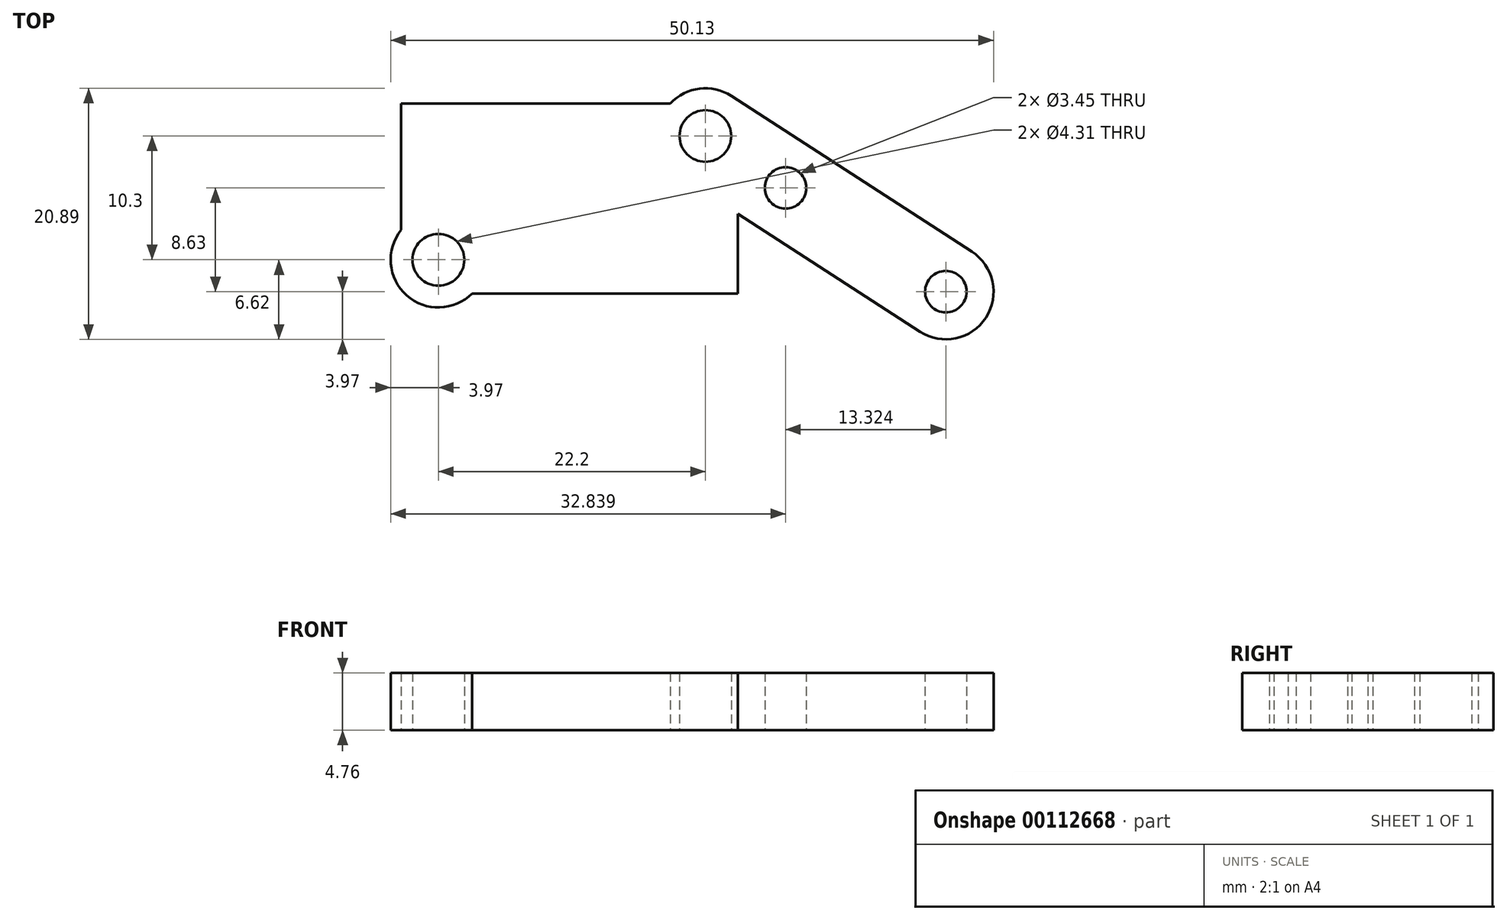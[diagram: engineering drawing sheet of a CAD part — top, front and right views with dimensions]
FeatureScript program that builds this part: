
annotation { "Feature Type Name" : "Feature", "Feature Type Description" : "" }
export const myFeature = defineFeature(function(context is Context, id is Id, definition is map)
    precondition{}
    {
        {
            var Q0;
            Q0=qCreatedBy(makeId("Top.planeOp"),FACE);
            var sketch = newSketch(context, id + "F0", { "sketchPlane" : qUnion([Q0])});
            skLineSegment(sketch, "E0.left", {"start": v(0, 0) * mm, "end": v(0, -10.52) * mm});
            skLineSegment(sketch, "E1", {"start": v(25.3, 0) * mm, "end": v(25.3, -2.7) * mm, "construction": true});
            skLineSegment(sketch, "E2", {"start": v(3.1, -15.8) * mm, "end": v(3.1, -13) * mm, "construction": true});
            skLineSegment(sketch, "E3", {"start": v(3.1, -13) * mm, "end": v(0, -13) * mm, "construction": true});
            skCircle(sketch, "E4", {"center": v(3.1, -13) * mm, "radius": 2.15 * mm});
            skCircle(sketch, "E5", {"center": v(25.3, -2.7) * mm, "radius": 2.15 * mm});
            skLineSegment(sketch, "E6", {"start": v(5.91, -15.8) * mm, "end": v(28, -15.8) * mm});
            skLineSegment(sketch, "E7", {"start": v(0, 0) * mm, "end": v(22.4, 0) * mm});
            skLineSegment(sketch, "E8", {"start": v(25.3, -2.7) * mm, "end": v(3.1, -2.7) * mm, "construction": true});
            skLineSegment(sketch, "E9", {"start": v(3.1, -2.7) * mm, "end": v(3.1, -13) * mm, "construction": true});
            skLineSegment(sketch, "E10", {"start": v(27.46, 0.63) * mm, "end": v(47.45, -12.32) * mm});
            skLineSegment(sketch, "E11", {"start": v(47.45, -12.32) * mm, "end": v(43.14, -18.98) * mm, "construction": true});
            skLineSegment(sketch, "E12", {"start": v(43.14, -18.98) * mm, "end": v(28, -9.18) * mm});
            skLineSegment(sketch, "E13", {"start": v(28, -9.18) * mm, "end": v(28, -15.8) * mm});
            skCircle(sketch, "E14", {"center": v(31.97, -7.02) * mm, "radius": 3.97 * mm, "construction": true});
            skLineSegment(sketch, "E15", {"start": v(31.97, -7.02) * mm, "end": v(45.3, -15.65) * mm, "construction": true});
            skArc(sketch, "E16", {"start": v(43.14, -18.98) * mm, "mid": v(48.62, -17.8) * mm, "end": v(47.45, -12.32) * mm});
            skCircle(sketch, "E17", {"center": v(45.3, -15.65) * mm, "radius": 1.73 * mm});
            skCircle(sketch, "E18", {"center": v(31.97, -7.02) * mm, "radius": 1.73 * mm});
            skArc(sketch, "E19", {"start": v(0, -10.52) * mm, "mid": v(0.46, -15.96) * mm, "end": v(5.91, -15.8) * mm});
            skArc(sketch, "E20", {"start": v(27.46, 0.63) * mm, "mid": v(24.8, 1.24) * mm, "end": v(22.4, 0) * mm});
            skSolve(sketch);
        }
        {
            var Q0;
            Q0=makeQuery(id+"F0.imprint","IMPRINT",FACE,{"disambiguationData":[TD([[makeQuery(id+"F0.imprint","IMPRINT",EDGE,{"derivedFrom":sQuery(id+"F0.wireOp",EDGE,"E0.bottom")}),-1.0]])]});
            var Q1;
            Q1=makeQuery(id+"F0.imprint","IMPRINT",FACE,{"disambiguationData":[TD([[makeQuery(id+"F0.imprint","IMPRINT",EDGE,{"derivedFrom":sQuery(id+"F0.wireOp",EDGE,"E0.left")}),1.0]])]});
            extrude(context, id + "F1", {"entities" : qUnion([Q0, Q1]), "depth" : 4.76 * mm});
        }
    });
